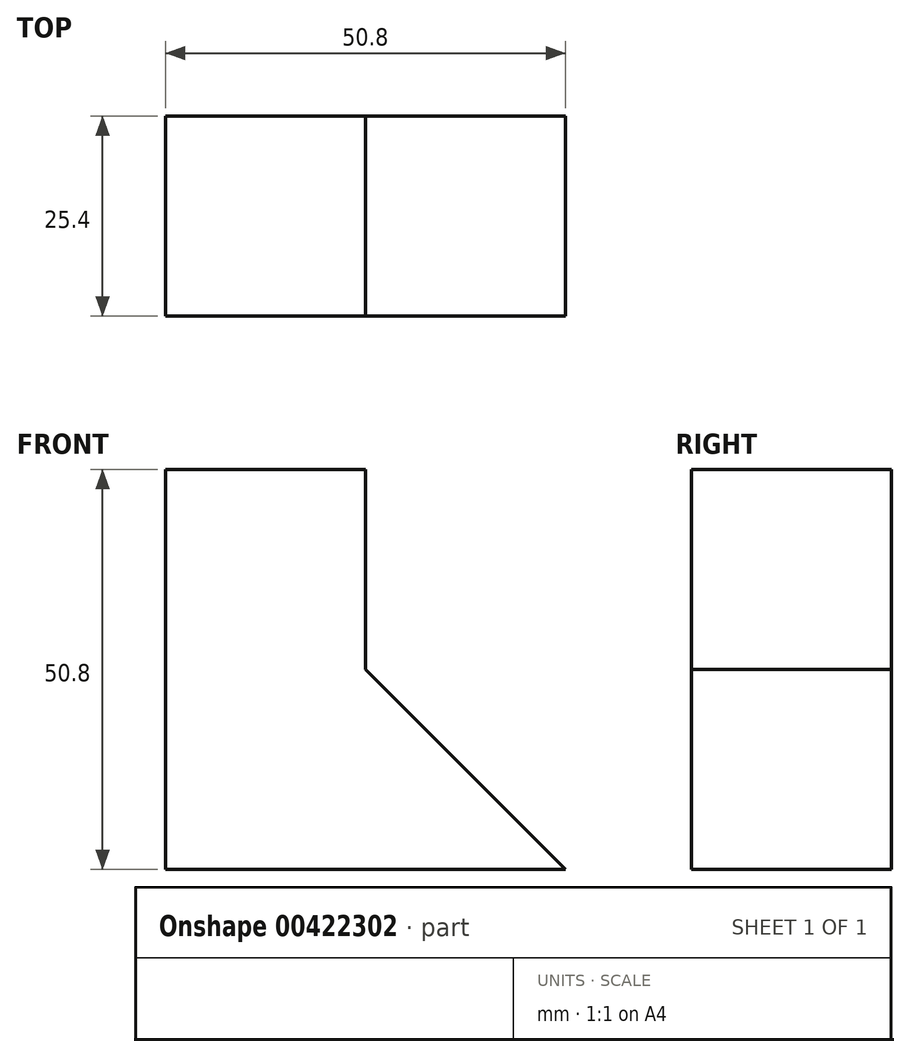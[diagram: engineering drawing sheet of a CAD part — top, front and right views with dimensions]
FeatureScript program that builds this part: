
annotation { "Feature Type Name" : "Feature", "Feature Type Description" : "" }
export const myFeature = defineFeature(function(context is Context, id is Id, definition is map)
    precondition{}
    {
        {
            var Q0;
            Q0=qCreatedBy(makeId("Front.planeOp"),FACE);
            var sketch = newSketch(context, id + "F0", { "sketchPlane" : qUnion([Q0])});
            skLineSegment(sketch, "E0", {"start": v(-56.67, -25.4) * mm, "end": v(-5.87, -25.4) * mm});
            skLineSegment(sketch, "E1", {"start": v(-56.67, -25.4) * mm, "end": v(-56.67, 25.4) * mm});
            skLineSegment(sketch, "E2", {"start": v(-56.67, 25.4) * mm, "end": v(-31.27, 25.4) * mm});
            skLineSegment(sketch, "E3", {"start": v(-31.27, 25.4) * mm, "end": v(-31.27, 0) * mm});
            skLineSegment(sketch, "E4", {"start": v(-31.27, 0) * mm, "end": v(-5.87, -25.4) * mm});
            skSolve(sketch);
        }
        {
            var Q0;
            Q0 = qSketchRegion(id + "F0", true);
            extrude(context, id + "F1", {"entities" : qUnion([Q0]), "depth" : 25.4 * mm});
        }
    });
